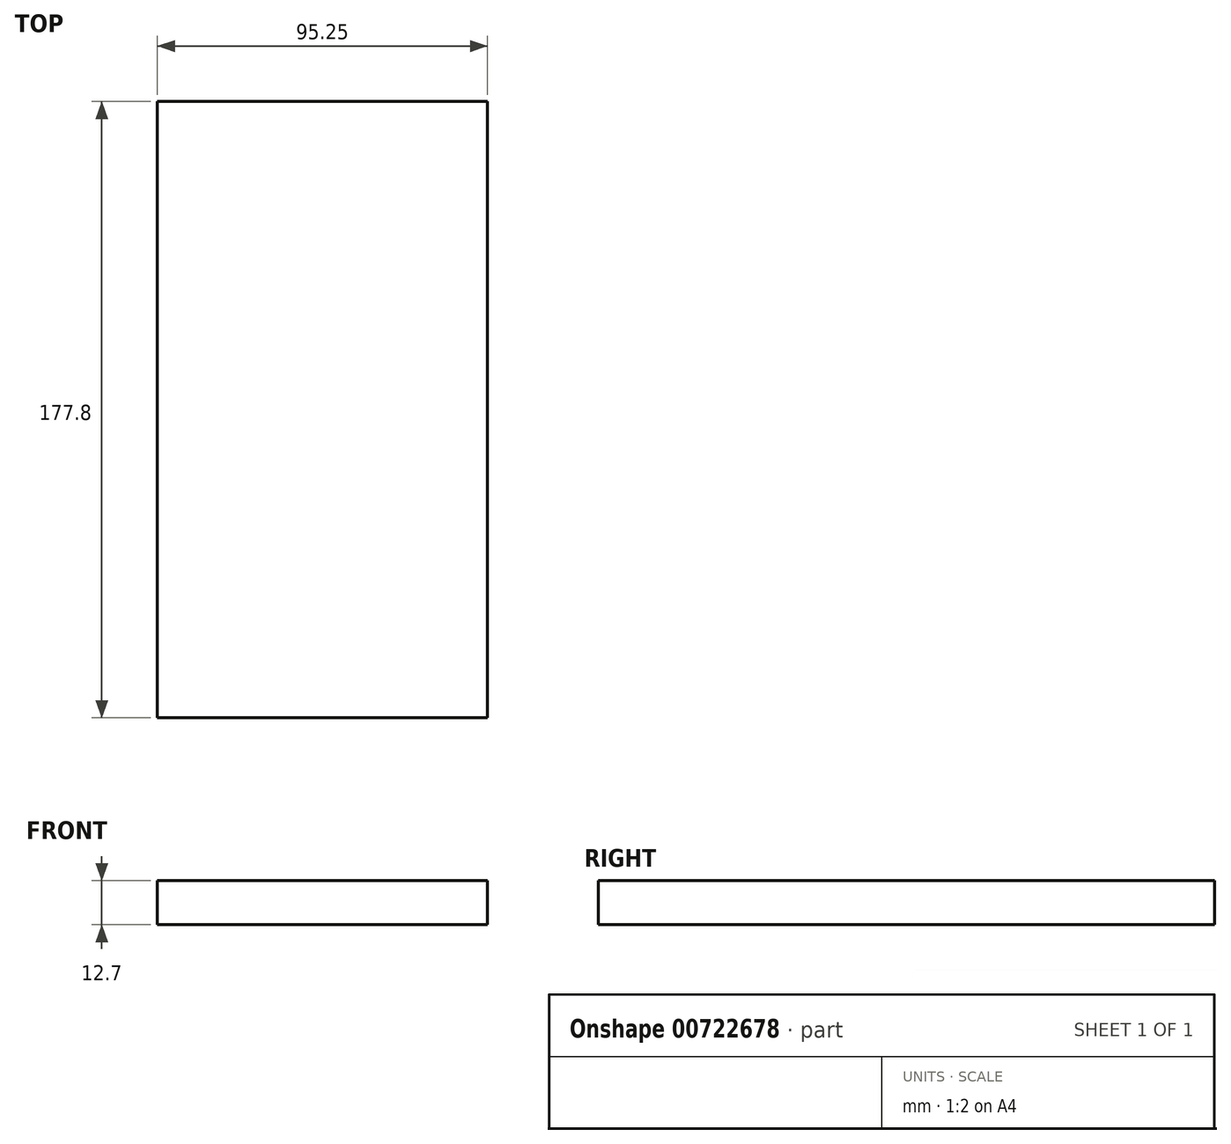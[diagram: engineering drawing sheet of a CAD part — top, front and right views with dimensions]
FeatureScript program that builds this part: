
annotation { "Feature Type Name" : "Feature", "Feature Type Description" : "" }
export const myFeature = defineFeature(function(context is Context, id is Id, definition is map)
    precondition{}
    {
        {
            var Q0;
            Q0=qCreatedBy(makeId("Front.planeOp"),FACE);
            var sketch = newSketch(context, id + "F0", { "sketchPlane" : qUnion([Q0])});
            skLineSegment(sketch, "E0.bottom", {"start": v(0, 0) * mm, "end": v(95.25, 0) * mm});
            skLineSegment(sketch, "E0.top", {"start": v(0, 12.7) * mm, "end": v(95.25, 12.7) * mm});
            skLineSegment(sketch, "E0.left", {"start": v(0, 0) * mm, "end": v(0, 12.7) * mm});
            skLineSegment(sketch, "E0.right", {"start": v(95.25, 0) * mm, "end": v(95.25, 12.7) * mm});
            skSolve(sketch);
        }
        {
            var Q0;
            Q0=qSketchRegion(id+"F0",true);
            extrude(context, id + "F1", {"entities" : qUnion([Q0]), "oppositeDirection" : true, "depth" : 177.8 * mm, "offsetDistance" : 25.4 * mm});
        }
    });
